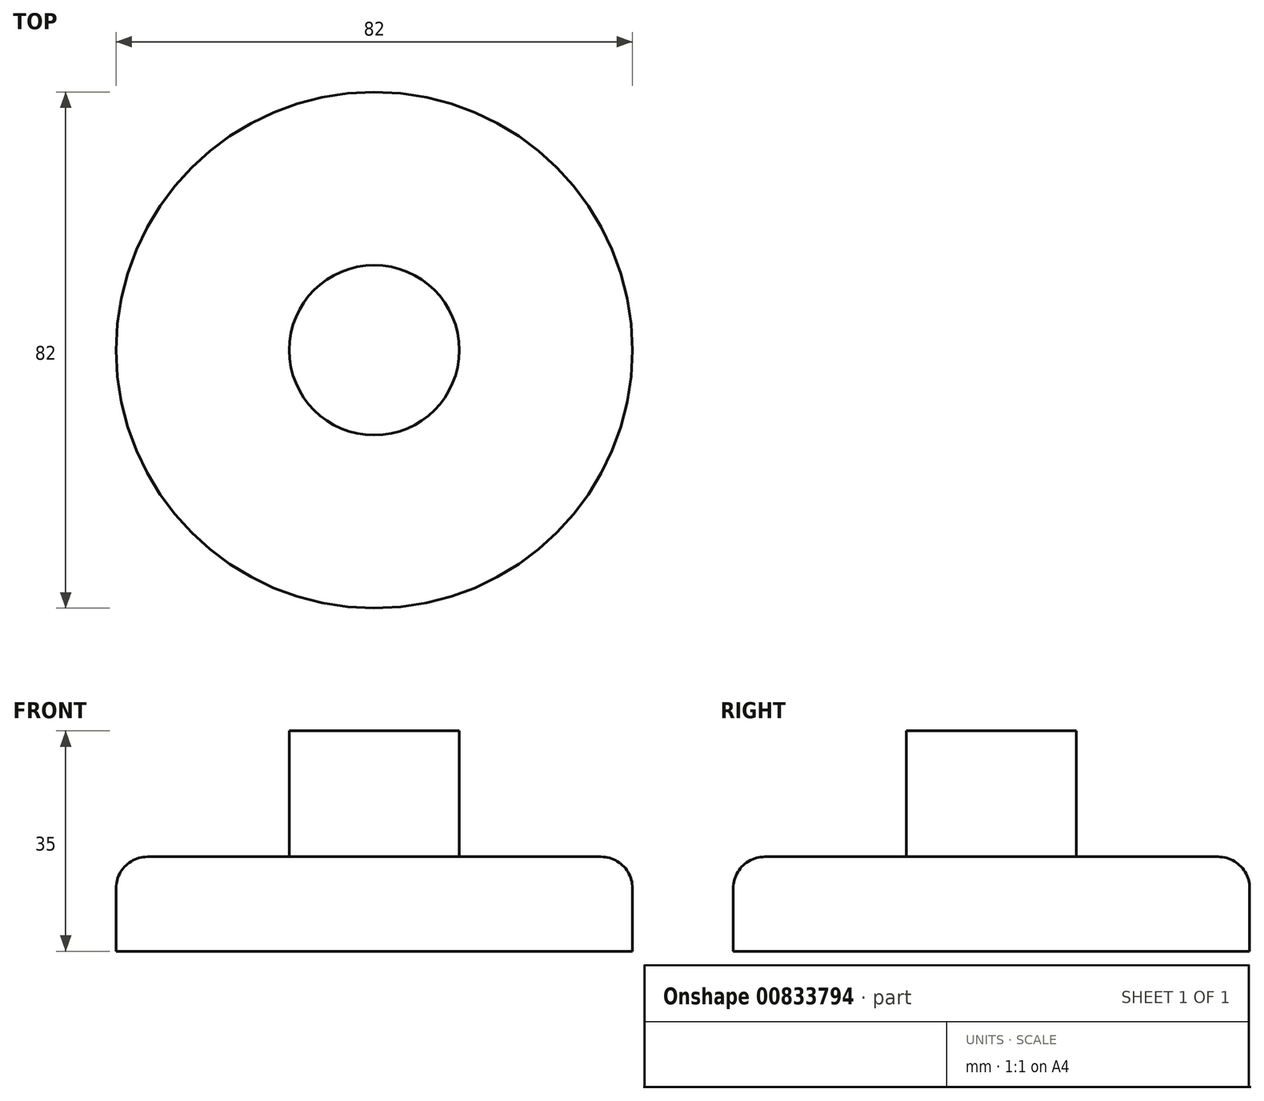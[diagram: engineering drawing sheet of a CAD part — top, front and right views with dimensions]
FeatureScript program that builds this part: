
annotation { "Feature Type Name" : "Feature", "Feature Type Description" : "" }
export const myFeature = defineFeature(function(context is Context, id is Id, definition is map)
    precondition{}
    {
        {
            var Q0;
            Q0=qCreatedBy(makeId("Top.planeOp"),FACE);
            var sketch = newSketch(context, id + "F0", { "sketchPlane" : qUnion([Q0])});
            skCircle(sketch, "E0", {"center": v(0, 0) * mm, "radius": 41 * mm});
            skCircle(sketch, "E1", {"center": v(0, 0) * mm, "radius": 13.5 * mm});
            skSolve(sketch);
        }
        {
            var Q0;
            Q0=makeQuery(id+"F0.imprint","IMPRINT",FACE,{"disambiguationData":[TD([[makeQuery(id+"F0.imprint","IMPRINT",EDGE,{"derivedFrom":sQuery(id+"F0.wireOp",EDGE,"E0")}),1.0]])]});
            extrude(context, id + "F1", {"entities" : qUnion([Q0]), "depth" : 15 * mm, "offsetDistance" : 25 * mm});
        }
        {
            var Q0;
            Q0=makeQuery(id+"F0.imprint","IMPRINT",FACE,{"disambiguationData":[TD([[makeQuery(id+"F0.imprint","IMPRINT",EDGE,{"derivedFrom":sQuery(id+"F0.wireOp",EDGE,"E1")}),1.0]])]});
            extrude(context, id + "F2", {"entities" : qUnion([Q0]), "operationType" : NewBodyOperationType.ADD, "depth" : 35 * mm, "offsetDistance" : 25 * mm});
        }
        {
            var Q0;
            Q0=makeQuery(id+"F1.opExtrude","CAP_EDGE",EDGE,{"disambiguationData":[OSD([sQuery(id+"F0.wireOp",EDGE,"E0")])],"isStart":false});
            var Q1;
            Q1=makeQuery(id+"F1.opExtrude","CAP_EDGE",EDGE,{"disambiguationData":[OSD([sQuery(id+"F0.wireOp",EDGE,"E1")])],"isStart":false});
            fillet(context, id + "F3", {"entities" : qUnion([Q0, Q1]), "radius" : 5 * mm, "tangentPropagation" : true, "allowEdgeOverflow" : false});
        }
    });
